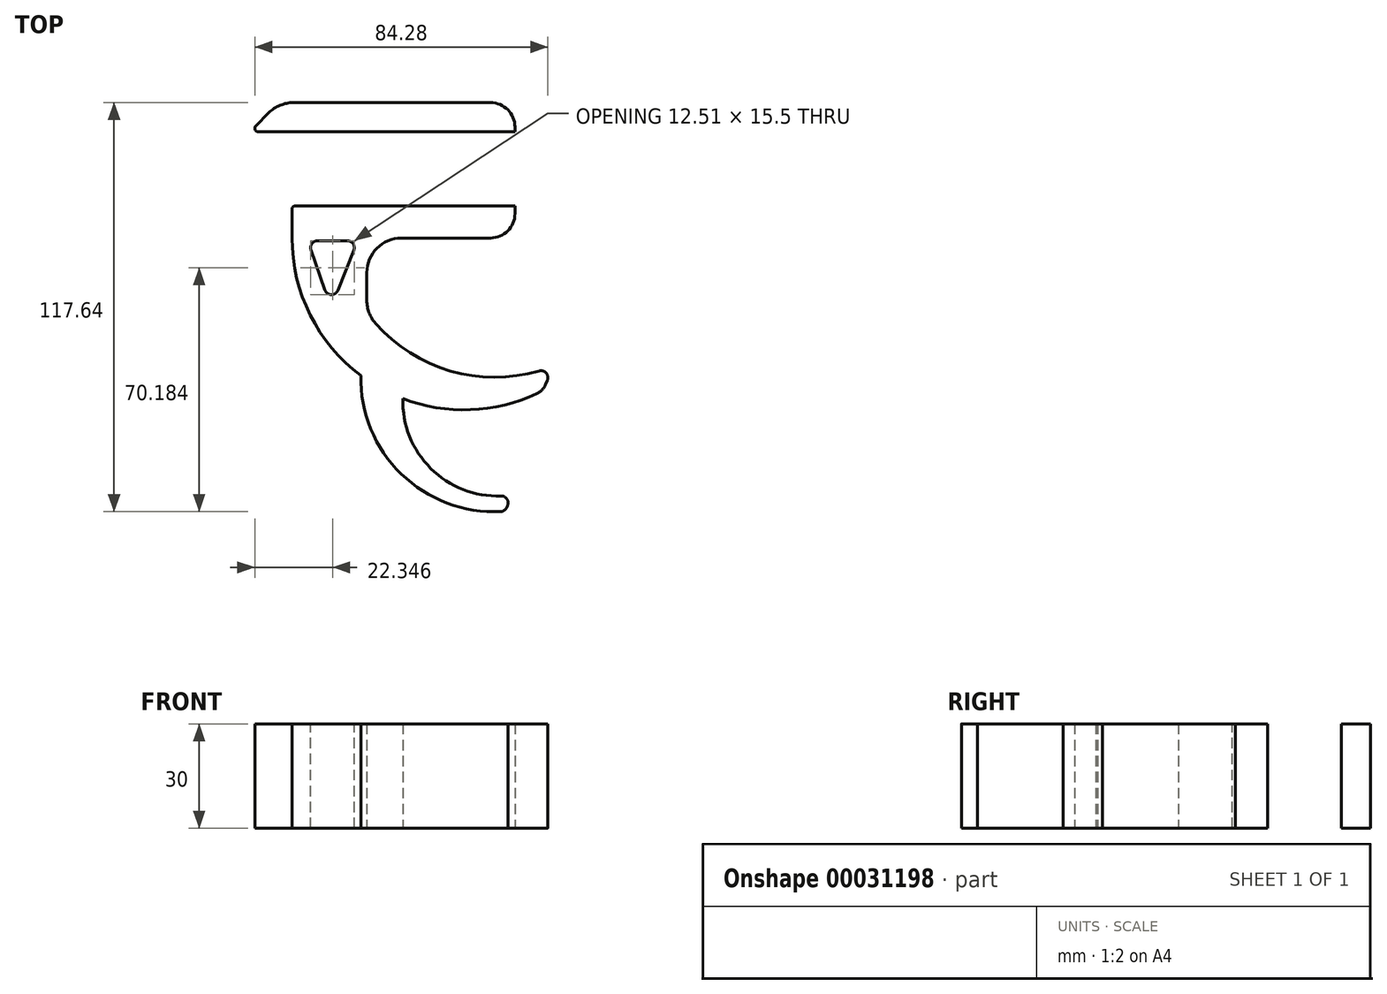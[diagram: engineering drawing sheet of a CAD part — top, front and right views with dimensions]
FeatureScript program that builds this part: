
annotation { "Feature Type Name" : "Feature", "Feature Type Description" : "" }
export const myFeature = defineFeature(function(context is Context, id is Id, definition is map)
    precondition{}
    {
        {
            var Q0;
            Q0=qCreatedBy(makeId("Top.planeOp"),FACE);
            var sketch = newSketch(context, id + "F0", { "sketchPlane" : qUnion([Q0])});
            skLineSegment(sketch, "E0.bottom", {"start": v(-54.42, 17.03) * mm, "end": v(23.43, 17.03) * mm});
            skLineSegment(sketch, "E0.top", {"start": v(-54.42, 8.63) * mm, "end": v(23.43, 8.63) * mm});
            skLineSegment(sketch, "E0.left", {"start": v(-54.42, 17.03) * mm, "end": v(-54.42, 8.63) * mm});
            skLineSegment(sketch, "E0.right", {"start": v(23.43, 17.03) * mm, "end": v(23.43, 8.63) * mm});
            skLineSegment(sketch, "E1.bottom", {"start": v(23.43, 8.63) * mm, "end": v(12.9, 8.63) * mm});
            skLineSegment(sketch, "E1.top", {"start": v(23.43, -12.63) * mm, "end": v(12.9, -12.63) * mm});
            skLineSegment(sketch, "E1.left", {"start": v(23.43, 8.63) * mm, "end": v(23.43, -12.63) * mm});
            skLineSegment(sketch, "E1.right", {"start": v(12.9, 8.63) * mm, "end": v(12.9, -12.63) * mm});
            skLineSegment(sketch, "E2.bottom", {"start": v(23.43, -12.63) * mm, "end": v(-40.7, -12.63) * mm});
            skLineSegment(sketch, "E2.top", {"start": v(23.43, -21.9) * mm, "end": v(-40.7, -21.9) * mm});
            skLineSegment(sketch, "E2.left", {"start": v(23.43, -12.63) * mm, "end": v(23.43, -21.9) * mm});
            skLineSegment(sketch, "E2.right", {"start": v(-40.7, -12.63) * mm, "end": v(-40.7, -21.9) * mm});
            skArc(sketch, "E3", {"start": v(-40.7, -21.9) * mm, "mid": v(-16.93, -64.13) * mm, "end": v(31.52, -65.76) * mm});
            skArc(sketch, "E4", {"start": v(-27.75, -21.9) * mm, "mid": v(-5.7, -55.55) * mm, "end": v(34.41, -58.72) * mm});
            skLineSegment(sketch, "E5", {"start": v(31.52, -65.76) * mm, "end": v(34.41, -58.72) * mm});
            skLineSegment(sketch, "E6", {"start": v(-19.18, -43.37) * mm, "end": v(-19.18, -21.9) * mm});
            skArc(sketch, "E7", {"start": v(-20.89, -61.46) * mm, "mid": v(-8.83, -90.16) * mm, "end": v(20.54, -100.5) * mm});
            skArc(sketch, "E8", {"start": v(-8.81, -68.1) * mm, "mid": v(0.45, -89.32) * mm, "end": v(22.7, -95.74) * mm});
            skLineSegment(sketch, "E9", {"start": v(20.54, -100.5) * mm, "end": v(22.7, -95.74) * mm});
            skSolve(sketch);
        }
        {
            var Q0;
            Q0=makeQuery(id+"F0.imprint","IMPRINT",FACE,{"disambiguationData":[TD([[makeQuery(id+"F0.imprint","IMPRINT",EDGE,{"derivedFrom":sQuery(id+"F0.wireOp",EDGE,"E0.bottom")}),-1.0]])]});
            var Q1;
            Q1=makeQuery(id+"F0.imprint","IMPRINT",FACE,{"disambiguationData":[TD([[makeQuery(id+"F0.imprint","IMPRINT",EDGE,{"derivedFrom":sQuery(id+"F0.wireOp",EDGE,"E1.bottom")}),1.0]])]});
            var Q2;
            {var subQ1=sQuery(id+"F0.wireOp",EDGE,"E2.left");Q2=makeQuery(id+"F0.imprint","IMPRINT",FACE,{"disambiguationData":[TD([[makeQuery(id+"F0.imprint","IMPRINT",EDGE,{"derivedFrom":subQ1}),-1.0]])]});}
            var Q3;
            {var subQ0=sQuery(id+"F0.wireOp",EDGE,"E6");Q3=makeQuery(id+"F0.imprint","IMPRINT",FACE,{"disambiguationData":[TD([[makeQuery(id+"F0.imprint","IMPRINT",EDGE,{"derivedFrom":subQ0}),1.0]])]});}
            var Q4;
            {var subQ0=sQuery(id+"F0.wireOp",EDGE,"E5");Q4=makeQuery(id+"F0.imprint","IMPRINT",FACE,{"disambiguationData":[TD([[makeQuery(id+"F0.imprint","IMPRINT",EDGE,{"derivedFrom":subQ0}),1.0]])]});}
            var Q5;
            {var subQ0=sQuery(id+"F0.wireOp",EDGE,"E7");Q5=makeQuery(id+"F0.imprint","IMPRINT",FACE,{"disambiguationData":[TD([[makeQuery(id+"F0.imprint","IMPRINT",EDGE,{"derivedFrom":subQ0}),1.0]])]});}
            extrude(context, id + "F1", {"entities" : qUnion([Q0, Q1, Q2, Q3, Q4, Q5]), "depth" : 30 * mm});
        }
        {
            var Q0;
            Q0=makeQuery(id+"F1.opExtrude","SWEPT_EDGE",EDGE,{"disambiguationData":[OSD([sQuery(id+"F0.wireOp",EDGE,"E3"),sQuery(id+"F0.wireOp",EDGE,"E5")])]});
            fillet(context, id + "F2", {"entities" : qUnion([Q0]), "radius" : 5 * mm, "tangentPropagation" : true, "allowEdgeOverflow" : false});
        }
        {
            var Q0;
            Q0=makeQuery(id+"F1.opExtrude","SWEPT_EDGE",EDGE,{"disambiguationData":[OSD([sQuery(id+"F0.wireOp",EDGE,"E4"),sQuery(id+"F0.wireOp",EDGE,"E5")])]});
            fillet(context, id + "F3", {"entities" : qUnion([Q0]), "radius" : 2 * mm, "tangentPropagation" : true, "allowEdgeOverflow" : false});
        }
        {
            var Q0;
            Q0=makeQuery(id+"F1.opExtrude","SWEPT_EDGE",EDGE,{"disambiguationData":[OSD([sQuery(id+"F0.wireOp",EDGE,"E8"),sQuery(id+"F0.wireOp",EDGE,"E9")])]});
            fillet(context, id + "F4", {"entities" : qUnion([Q0]), "radius" : 2 * mm, "tangentPropagation" : true, "allowEdgeOverflow" : false});
        }
        {
            var Q0;
            Q0=makeQuery(id+"F1.opExtrude","SWEPT_EDGE",EDGE,{"disambiguationData":[OSD([sQuery(id+"F0.wireOp",EDGE,"E7"),sQuery(id+"F0.wireOp",EDGE,"E9")])]});
            fillet(context, id + "F5", {"entities" : qUnion([Q0]), "radius" : 2 * mm, "tangentPropagation" : true, "allowEdgeOverflow" : false});
        }
        {
            var Q0;
            Q0=makeQuery(id+"F1.opExtrude","SWEPT_EDGE",EDGE,{"disambiguationData":[OSD([sQuery(id+"F0.wireOp",EDGE,"E2.top"),sQuery(id+"F0.wireOp",EDGE,"E2.left")])]});
            var Q1;
            Q1=makeQuery(id+"F1.opExtrude","SWEPT_EDGE",EDGE,{"disambiguationData":[OSD([sQuery(id+"F0.wireOp",EDGE,"E0.bottom"),sQuery(id+"F0.wireOp",EDGE,"E0.right")])]});
            fillet(context, id + "F6", {"entities" : qUnion([Q0, Q1]), "radius" : 7 * mm, "tangentPropagation" : true, "allowEdgeOverflow" : false});
        }
        {
            var Q0;
            Q0=makeQuery(id+"F1.opExtrude","SWEPT_EDGE",EDGE,{"disambiguationData":[OSD([sQuery(id+"F0.wireOp",EDGE,"E0.bottom"),sQuery(id+"F0.wireOp",EDGE,"E0.left")])]});
            chamfer(context, id + "F7", {"entities" : qUnion([Q0]), "width" : 10 * mm, "tangentPropagation" : true});
        }
        {
            var Q0;
            {var subQ0=sQuery(id+"F0.wireOp",EDGE,"E0.bottom");Q0=makeQuery(id+"F7.opChamfer","BLEND_EDGE",EDGE,{"blendedFrom":[makeQuery(id+"F1.opExtrude","SWEPT_EDGE",EDGE,{"disambiguationData":[OSD([subQ0,sQuery(id+"F0.wireOp",EDGE,"E0.left")])]}),makeQuery(id+"F1.opExtrude","SWEPT_FACE",FACE,{"disambiguationData":[OSD([subQ0])]})],"blendedInto":[makeQuery(id+"F1.opExtrude","SWEPT_FACE",FACE,{"disambiguationData":[OSD([subQ0])]})]});}
            fillet(context, id + "F8", {"entities" : qUnion([Q0]), "radius" : 10 * mm, "tangentPropagation" : true, "allowEdgeOverflow" : false});
        }
        {
            var Q0;
            Q0=makeQuery(id+"F7.opChamfer","BLEND_EDGE",EDGE,{"blendedFrom":[makeQuery(id+"F1.opExtrude","SWEPT_EDGE",EDGE,{"disambiguationData":[OSD([sQuery(id+"F0.wireOp",EDGE,"E0.bottom"),sQuery(id+"F0.wireOp",EDGE,"E0.left")])]}),makeQuery(id+"F1.opExtrude","SWEPT_FACE",FACE,{"disambiguationData":[OSD([sQuery(id+"F0.wireOp",EDGE,"E0.top")])]})],"blendedInto":[makeQuery(id+"F1.opExtrude","SWEPT_FACE",FACE,{"disambiguationData":[OSD([sQuery(id+"F0.wireOp",EDGE,"E0.top")])]})]});
            var Q1;
            Q1=makeQuery(id+"F1.opExtrude","SWEPT_EDGE",EDGE,{"disambiguationData":[OSD([sQuery(id+"F0.wireOp",EDGE,"E2.bottom"),sQuery(id+"F0.wireOp",EDGE,"E2.right")])]});
            fillet(context, id + "F9", {"entities" : qUnion([Q0, Q1]), "radius" : 1 * mm, "tangentPropagation" : true, "allowEdgeOverflow" : false});
        }
        {
            var Q0;
            Q0=makeQuery(id+"F1.opExtrude","SWEPT_EDGE",EDGE,{"disambiguationData":[OSD([sQuery(id+"F0.wireOp",EDGE,"E2.top"),sQuery(id+"F0.wireOp",EDGE,"E6")])]});
            fillet(context, id + "F10", {"entities" : qUnion([Q0]), "radius" : 10 * mm, "tangentPropagation" : true, "allowEdgeOverflow" : false});
        }
        {
            var Q0;
            Q0=makeQuery(id+"F1.opExtrude","SWEPT_EDGE",EDGE,{"disambiguationData":[OSD([sQuery(id+"F0.wireOp",EDGE,"E4"),sQuery(id+"F0.wireOp",EDGE,"E6")])]});
            fillet(context, id + "F11", {"entities" : qUnion([Q0]), "radius" : 10 * mm, "tangentPropagation" : true, "allowEdgeOverflow" : false});
        }
        {
            var Q0;
            Q0=makeQuery(id+"F1.opExtrude","CAP_FACE",FACE,{"disambiguationData":[OSD([sQuery(id+"F0.wireOp",EDGE,"E0.bottom"),sQuery(id+"F0.wireOp",EDGE,"E0.top"),sQuery(id+"F0.wireOp",EDGE,"E0.left"),sQuery(id+"F0.wireOp",EDGE,"E0.right"),sQuery(id+"F0.wireOp",EDGE,"E1.left"),sQuery(id+"F0.wireOp",EDGE,"E1.right"),sQuery(id+"F0.wireOp",EDGE,"E2.bottom"),sQuery(id+"F0.wireOp",EDGE,"E2.top"),sQuery(id+"F0.wireOp",EDGE,"E2.left"),sQuery(id+"F0.wireOp",EDGE,"E2.right"),sQuery(id+"F0.wireOp",EDGE,"E3"),sQuery(id+"F0.wireOp",EDGE,"E4"),sQuery(id+"F0.wireOp",EDGE,"E5"),sQuery(id+"F0.wireOp",EDGE,"E6"),sQuery(id+"F0.wireOp",EDGE,"E7"),sQuery(id+"F0.wireOp",EDGE,"E8"),sQuery(id+"F0.wireOp",EDGE,"E9")])],"isStart":false});
            var sketch = newSketch(context, id + "F12", { "sketchPlane" : qUnion([Q0])});
            skLineSegment(sketch, "E10", {"start": v(-36.12, -22.68) * mm, "end": v(-21.84, -22.68) * mm});
            skLineSegment(sketch, "E11", {"start": v(-36.12, -22.68) * mm, "end": v(-29.5, -41.92) * mm});
            skLineSegment(sketch, "E12", {"start": v(-29.5, -41.92) * mm, "end": v(-21.84, -22.68) * mm});
            skSolve(sketch);
        }
        {
            var Q0;
            Q0=makeQuery(id+"F12.imprint","IMPRINT",FACE,{"disambiguationData":[TD([[makeQuery(id+"F12.imprint","IMPRINT",EDGE,{"derivedFrom":sQuery(id+"F12.wireOp",EDGE,"E10")}),-1.0]])]});
            extrude(context, id + "F13", {"entities" : qUnion([Q0]), "operationType" : NewBodyOperationType.REMOVE, "oppositeDirection" : true, "depth" : 30 * mm});
        }
        {
            var Q0;
            Q0=makeQuery(id+"F13.boolean.opBoolean","COPY",EDGE,{"derivedFrom":makeQuery(id+"F13.opExtrude","SWEPT_EDGE",EDGE,{"disambiguationData":[OSD([sQuery(id+"F12.wireOp",EDGE,"E10"),sQuery(id+"F12.wireOp",EDGE,"E12")])]})});
            var Q1;
            Q1=makeQuery(id+"F13.boolean.opBoolean","COPY",EDGE,{"derivedFrom":makeQuery(id+"F13.opExtrude","SWEPT_EDGE",EDGE,{"disambiguationData":[OSD([sQuery(id+"F12.wireOp",EDGE,"E10"),sQuery(id+"F12.wireOp",EDGE,"E11")])]})});
            var Q2;
            Q2=makeQuery(id+"F13.boolean.opBoolean","COPY",EDGE,{"derivedFrom":makeQuery(id+"F13.opExtrude","SWEPT_EDGE",EDGE,{"disambiguationData":[OSD([sQuery(id+"F12.wireOp",EDGE,"E11"),sQuery(id+"F12.wireOp",EDGE,"E12")])]})});
            fillet(context, id + "F14", {"entities" : qUnion([Q0, Q1, Q2]), "radius" : 2 * mm, "tangentPropagation" : true, "allowEdgeOverflow" : false});
        }
    });
